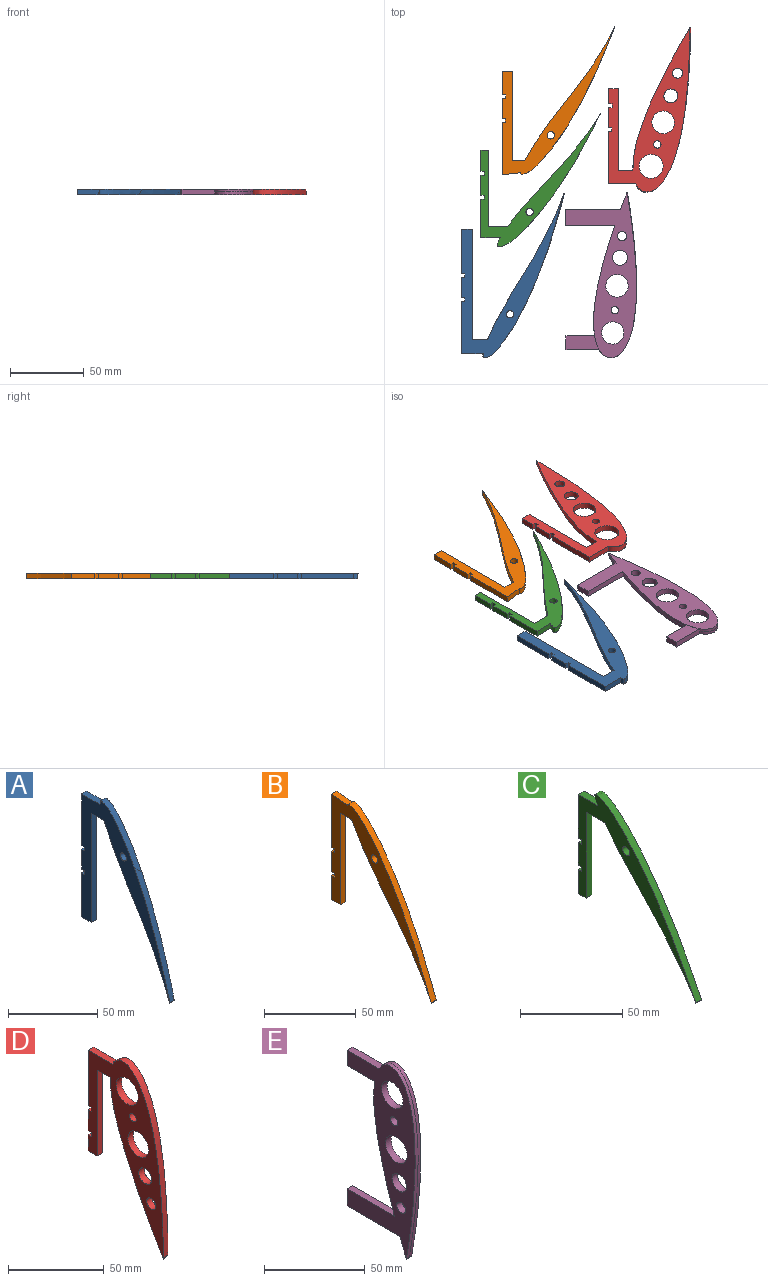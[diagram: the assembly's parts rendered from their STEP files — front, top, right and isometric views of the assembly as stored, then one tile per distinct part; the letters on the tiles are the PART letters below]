
ASSEMBLY  parts=5 mates=4
PART A: 22 faces, bbox 45.3x70.1x113 mm
  f0: plane 13.63x4mm, normal (0,1,0), area 54.5mm2, adj f2,f3,f16,f20
  f1: plane 30.21x4mm, normal (0,1,0), area 120.9mm2, adj f2,f3,f14,f15
  f2: plane 111.81x69.62mm, normal (1,0,0), area 1606.8mm2, adj f0,f1,f4,f5,f6,f7,f8,f9
  f3: plane 111.81x70.08mm, normal (-1,0,0), area 1626.7mm2, adj f0,f1,f4,f5,f6,f7,f8,f9
  f4: bspline ~45.15x18.4mm, area 55.7mm2, adj f2,f3,f7,f11
  f5: bspline ~45.15x5.68mm, area 12mm2, adj f2,f3,f8,f12
  f6: bspline ~77.91x27.83mm, area 341.3mm2, adj f2,f3,f7,f8
  f7: extruded ~88.41x46.76mm, area 406.7mm2, adj f2,f3,f4,f6
  f8: extruded ~36.82x28.71mm, area 183.3mm2, adj f2,f3,f5,f6
  f9: plane 75.11x4mm, normal (0,-1,0), area 300.4mm2, adj f2,f3,f10,f14
  f10: plane 10.21x4mm, normal (0,0,-1), area 40.9mm2, adj f2,f3,f9,f11
  f11: plane 4x0.12mm, normal (0,0.04,-1), area 0.2mm2, adj f2,f4,f10
  f12: plane 14.87x4.01mm, normal (0,0,1), area 59.1mm2, adj f2,f3,f5,f13
  f13: plane 35.47x4mm, normal (0,1,0), area 141.9mm2, adj f2,f3,f12,f18
  f14: plane 7.45x4mm, normal (0,0,-1), area 29.8mm2, adj f1,f2,f3,f9
  f15: plane 4x2.41mm, normal (0,0,1), area 9.6mm2, adj f1,f2,f3,f17
  f16: plane 4x2.41mm, normal (0,0,-1), area 9.6mm2, adj f0,f2,f3,f17
  f17: plane 4x2.64mm, normal (0,1,0), area 10.5mm2, adj f2,f3,f15,f16
  f18: plane 4x2.18mm, normal (0,0,-1), area 8.7mm2, adj f2,f3,f13,f19
  f19: plane 4x2.52mm, normal (0,1,0), area 10.1mm2, adj f2,f3,f18,f20
  f20: plane 4x2.18mm, normal (0,0,1), area 8.7mm2, adj f0,f2,f3,f19
  f21: cylinder r=2.5mm len=5mm, axis (1,0,0), area 62.8mm2, adj f2,f3
PART B: 17 faces, bbox 4x76.6x100.9 mm
  f0: plane 13.63x4mm, normal (0,1,0), area 54.5mm2, adj f2,f3,f11,f15
  f1: plane 15.99x4mm, normal (0,1,0), area 64mm2, adj f2,f3,f9,f10
  f2: plane 100.92x76.63mm, normal (-1,0,0), area 1781.6mm2, adj f0,f1,f4,f5,f6,f7,f8,f9
  f3: plane 100.92x76.63mm, normal (1,0,0), area 1781.6mm2, adj f0,f1,f4,f5,f6,f7,f8,f9
  f4: extruded ~98.54x63.72mm, area 931.5mm2, adj f2,f3,f5,f7
  f5: plane 8.5x4mm, normal (0,0,-1), area 34mm2, adj f2,f3,f4,f6
  f6: plane 60.89x4mm, normal (0,-1,0), area 243.6mm2, adj f2,f3,f5,f9
  f7: plane 12.47x4mm, normal (0,-0.11,0.99), area 50.2mm2, adj f2,f3,f4,f8
  f8: plane 35.47x4mm, normal (0,1,0), area 141.9mm2, adj f2,f3,f7,f13
  f9: plane 6.86x4mm, normal (0,0,-1), area 27.4mm2, adj f1,f2,f3,f6
  f10: plane 4x2.41mm, normal (0,0,1), area 9.6mm2, adj f1,f2,f3,f12
  f11: plane 4x2.41mm, normal (0,0,-1), area 9.6mm2, adj f0,f2,f3,f12
  f12: plane 4x2.64mm, normal (0,1,0), area 10.5mm2, adj f2,f3,f10,f11
  f13: plane 4x2.18mm, normal (0,0,-1), area 8.7mm2, adj f2,f3,f8,f14
  f14: plane 4x2.52mm, normal (0,1,0), area 10.1mm2, adj f2,f3,f13,f15
  f15: plane 4x2.18mm, normal (0,0,1), area 8.7mm2, adj f0,f2,f3,f14
  f16: cylinder r=2.5mm len=5mm, axis (1,0,0), area 62.8mm2, adj f2,f3
PART C: 17 faces, bbox 4x81.2x90.4 mm
  f0: plane 13.63x4mm, normal (0,1,0), area 54.5mm2, adj f2,f3,f11,f15
  f1: plane 14.53x4mm, normal (0,1,0), area 58.1mm2, adj f2,f3,f9,f10
  f2: plane 90.41x81.16mm, normal (-1,0,0), area 1564.6mm2, adj f0,f1,f4,f5,f6,f7,f8,f9
  f3: plane 90.41x81.16mm, normal (1,0,0), area 1564.6mm2, adj f0,f1,f4,f5,f6,f7,f8,f9
  f4: extruded ~88.59x68.13mm, area 891.7mm2, adj f2,f3,f6,f7
  f5: plane 51.72x4mm, normal (0,-1,0), area 206.9mm2, adj f2,f3,f6,f9
  f6: plane 12.91x4mm, normal (0,0,-1), area 51.6mm2, adj f2,f3,f4,f5
  f7: plane 13.23x4mm, normal (0,0,1), area 52.9mm2, adj f2,f3,f4,f8
  f8: plane 26.11x4mm, normal (0,1,0), area 104.4mm2, adj f2,f3,f7,f13
  f9: plane 5.3x4mm, normal (0,0,-1), area 21.2mm2, adj f1,f2,f3,f5
  f10: plane 4x2.41mm, normal (0,0,1), area 9.6mm2, adj f1,f2,f3,f12
  f11: plane 4x2.41mm, normal (0,0,-1), area 9.6mm2, adj f0,f2,f3,f12
  f12: plane 4x2.64mm, normal (0,1,0), area 10.5mm2, adj f2,f3,f10,f11
  f13: plane 4x2.18mm, normal (0,0,-1), area 8.7mm2, adj f2,f3,f8,f14
  f14: plane 4x2.52mm, normal (0,1,0), area 10.1mm2, adj f2,f3,f13,f15
  f15: plane 4x2.18mm, normal (0,0,1), area 8.7mm2, adj f0,f2,f3,f14
  f16: cylinder r=2.5mm len=5mm, axis (1,0,0), area 62.8mm2, adj f2,f3
PART D: 22 faces, bbox 7.7x59.4x115.4 mm
  f0: plane 13.63x4mm, normal (0,1,0), area 54.5mm2, adj f2,f3,f12,f16
  f1: plane 10.25x4mm, normal (0,1,0), area 41mm2, adj f2,f3,f9,f11
  f2: plane 114.8x58.74mm, normal (1,0,0), area 2187mm2, adj f0,f1,f4,f5,f6,f7,f8,f9
  f3: plane 112.08x56.05mm, normal (-1,0,0), area 2185.2mm2, adj f0,f1,f4,f5,f7,f8,f9,f10
  f4: bspline ~110.83x39.21mm, area 943.9mm2, adj f2,f3,f6,f7
  f5: plane 9.79x4mm, normal (0,0,-1), area 39.2mm2, adj f2,f3,f6,f10
  f6: plane 4x0.13mm, normal (0,0.12,-0.99), area 0.2mm2, adj f2,f4,f5
  f7: plane 18.52x4.01mm, normal (0,0,1), area 73.5mm2, adj f2,f3,f4,f8
  f8: plane 35.47x4mm, normal (0,1,0), area 141.9mm2, adj f2,f3,f7,f14
  f9: plane 6.65x4mm, normal (0,0,-1), area 26.6mm2, adj f1,f2,f3,f10
  f10: plane 55.15x4mm, normal (0,-1,0), area 220.6mm2, adj f2,f3,f5,f9
  f11: plane 4x2.41mm, normal (0,0,1), area 9.6mm2, adj f1,f2,f3,f13
  f12: plane 4x2.41mm, normal (0,0,-1), area 9.6mm2, adj f0,f2,f3,f13
  f13: plane 4x2.64mm, normal (0,1,0), area 10.5mm2, adj f2,f3,f11,f12
  f14: plane 4x2.18mm, normal (0,0,-1), area 8.7mm2, adj f2,f3,f8,f15
  f15: plane 4x2.52mm, normal (0,1,0), area 10.1mm2, adj f2,f3,f14,f16
  f16: plane 4x2.18mm, normal (0,0,1), area 8.7mm2, adj f0,f2,f3,f15
  f17: cylinder r=2.5mm len=5mm, axis (1,0,0), area 62.8mm2, adj f2,f3
  f18: cylinder r=3.39mm len=6.78mm, axis (1,0,0), area 85.1mm2, adj f2,f3
  f19: cylinder r=4.74mm len=9.49mm, axis (1,0,0), area 119.2mm2, adj f2,f3
  f20: cylinder r=7.68mm len=15.35mm, axis (1,0,0), area 192.9mm2, adj f2,f3
  f21: cylinder r=8.15mm len=16.3mm, axis (1,0,0), area 204.8mm2, adj f2,f3
PART E: 18 faces, bbox 4.7x48.7x112.9 mm
  f0: extruded ~75.11x14.64mm, area 154mm2, adj f1,f4,f5,f11
  f1: bspline ~110.41x29.22mm, area 457.8mm2, adj f0,f2,f3,f5,f7,f8
  f2: extruded ~111.32x25.54mm, area 283.2mm2, adj f1,f4,f7,f9
  f3: plane 112.47x48.21mm, normal (1,0,0), area 1981.7mm2, adj f1,f5,f6,f7,f13,f14,f15,f16
  f4: plane 112.75x48.67mm, normal (-1,0,0), area 2173.8mm2, adj f0,f2,f5,f6,f7,f9,f10,f11
  f5: plane 33.32x4mm, normal (0,0,1), area 133.1mm2, adj f0,f1,f3,f4,f6
  f6: plane 10.35x4mm, normal (0,1,0), area 41.4mm2, adj f3,f4,f5,f7
  f7: plane 37.1x4mm, normal (0,0,-1), area 148.2mm2, adj f1,f2,f3,f4,f6
  f8: extruded ~9.36x2.99mm, area 19.7mm2, adj f1,f9,f11,f12
  f9: plane 22.39x4mm, normal (0,0,1), area 89.5mm2, adj f2,f4,f8,f10,f12
  f10: plane 9.36x4mm, normal (0,1,0), area 37.4mm2, adj f4,f9,f11,f12
  f11: plane 19.39x4mm, normal (0,0,-1), area 77.6mm2, adj f0,f4,f8,f10,f12
  f12: plane 22.51x9.5mm, normal (1,0,0), area 193mm2, adj f8,f9,f10,f11
  f13: cylinder r=2.5mm len=5mm, axis (1,0,0), area 62.8mm2, adj f3,f4
  f14: cylinder r=7.63mm len=15.26mm, axis (1,0,0), area 191.7mm2, adj f3,f4
  f15: cylinder r=7.58mm len=15.17mm, axis (1,0,0), area 190.6mm2, adj f3,f4
  f16: cylinder r=5.1mm len=10.21mm, axis (1,0,0), area 128.2mm2, adj f3,f4
  f17: cylinder r=3.1mm len=6.2mm, axis (1,0,0), area 77.9mm2, adj f3,f4
PLACE A rot(axis=(0.58,-0.58,0.58),120deg) t=(-117.12,-265.17,583.14)mm
PLACE B rot(axis=(0.58,-0.58,0.58),120deg) t=(-89.58,-143.76,685.14)mm
PLACE C rot(axis=(0.58,-0.58,0.58),120deg) t=(-103.91,-195.78,787.14)mm
PLACE D rot(axis=(0.58,-0.58,0.58),120deg) t=(-17.28,-149.97,481.14)mm
PLACE E rot(axis=(0.58,-0.58,0.58),120deg) t=(-46.17,-262.42,381.14)mm
MATE planar D.f2 <-> E.f3  axis (0,0,1) through (-20.4,-137.55,181.14)mm
MATE planar A.f2 <-> D.f2  axis (0,0,1) through (-106.33,-257.84,181.14)mm
MATE planar C.f3 <-> B.f3  axis (0,0,1) through (-108.65,-187.17,181.14)mm
MATE planar B.f3 <-> A.f2  axis (0,0,1) through (-96.64,-135.29,181.14)mm
